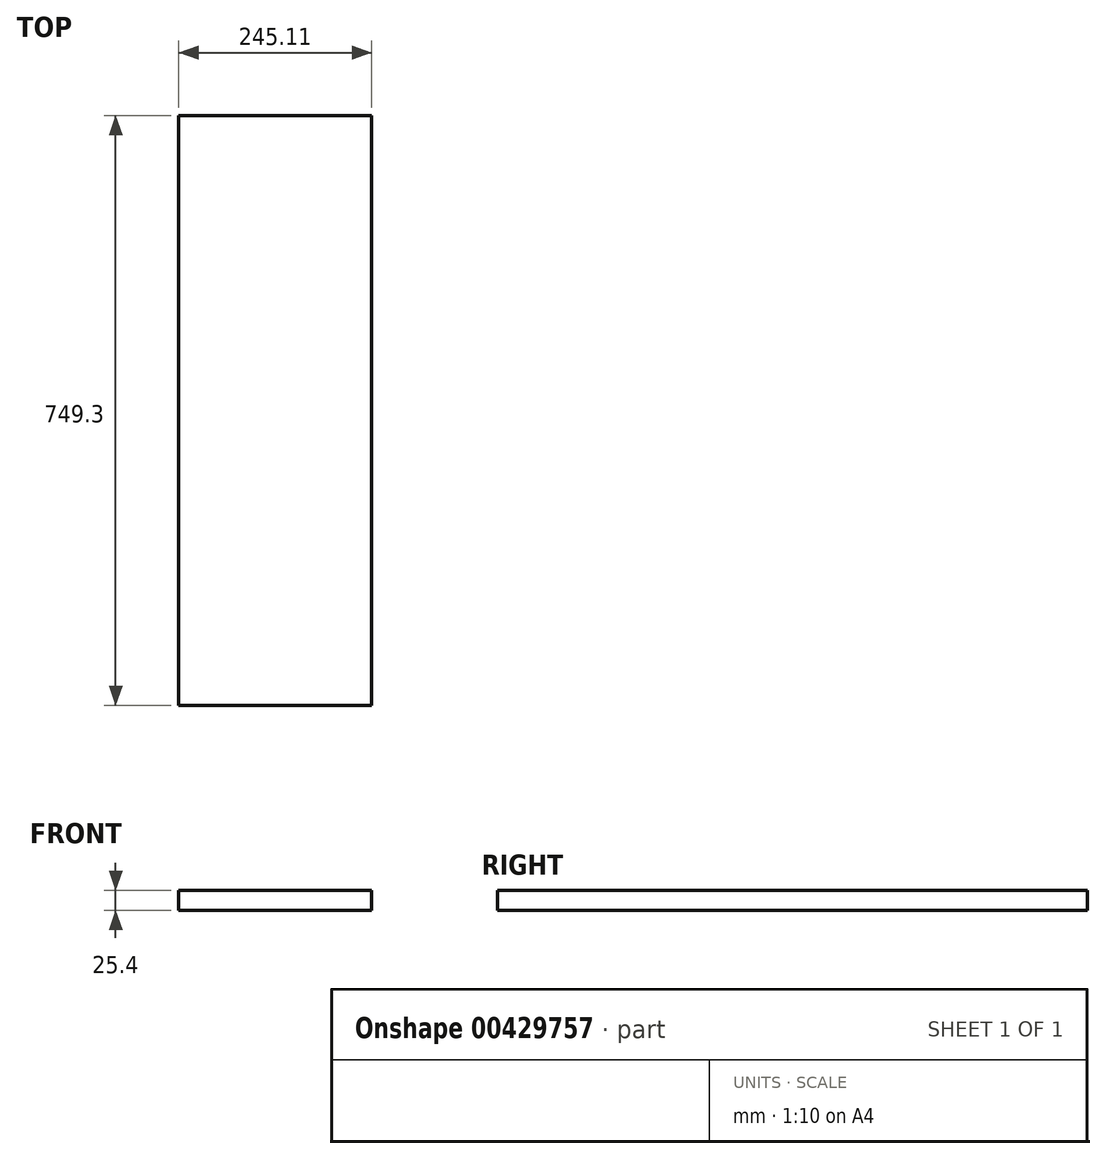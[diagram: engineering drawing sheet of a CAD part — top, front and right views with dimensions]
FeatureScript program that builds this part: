
annotation { "Feature Type Name" : "Feature", "Feature Type Description" : "" }
export const myFeature = defineFeature(function(context is Context, id is Id, definition is map)
    precondition{}
    {
        {
            var Q0;
            Q0=qCreatedBy(makeId("Top.planeOp"),FACE);
            var sketch = newSketch(context, id + "F0", { "sketchPlane" : qUnion([Q0])});
            skLineSegment(sketch, "E0", {"start": v(0, 0) * mm, "end": v(-245.11, 0) * mm});
            skLineSegment(sketch, "E1", {"start": v(0, -749.3) * mm, "end": v(0, 0) * mm});
            skLineSegment(sketch, "E2", {"start": v(-245.11, 0) * mm, "end": v(-245.1, -749.3) * mm});
            skLineSegment(sketch, "E3", {"start": v(-245.1, -749.3) * mm, "end": v(0, -749.3) * mm});
            skPoint(sketch, "E4.orphan", {"position": v(0, -635) * mm});
            skSolve(sketch);
        }
        {
            var Q0;
            Q0 = qSketchRegion(id + "F0", true);
            extrude(context, id + "F1", {"entities" : qUnion([Q0]), "depth" : 25.4 * mm});
        }
    });
